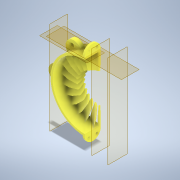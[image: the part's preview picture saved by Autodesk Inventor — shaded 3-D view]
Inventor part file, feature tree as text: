
AUTODESK INVENTOR PART (.ipt)
format: ipt  version: 2021.2 (Build 252289000, 289)  size: 1,402,368 bytes
history: native  units: in
note: dims shown in document units (in); Inventor stores cm internally (conversion verified against a paired STEP export)
features: sketch x11, extrude x10, plane x5, pattern_circular x3, fillet x2, loft x1, other x1
ambient origin geometry x8: Origin, YZ Plane, XZ Plane, XY Plane, X Axis, Y Axis, Z Axis, Center Point
bodies: Solid1 (feature_tree)
feature tree (33):
  extrude  "Extrusion1"  Depth=4.25in
  plane  "Work Plane2"
  extrude  "Extrusion3"  Depth=2.125in
  fillet  "Fillet1"  Radius=0.25in
  extrude  "Extrusion4"  Depth=0.5in TaperAngle=0.0deg
  pattern_circular  "Circular Pattern2"  Count=2 Angle=360.0deg
  plane  "Work Plane3"
  extrude  "Extrusion5"  Depth=1.0in
  extrude  "Extrusion6"  Depth=0.5in
  fillet  "Fillet2"  [1 undecoded]
  extrude  "Extrusion7"  Depth=0.5in TaperAngle=0.0deg
  pattern_circular  "Circular Pattern3"  [2 undecoded]
  plane  "Work Plane4"
  plane  "Work Plane6"
  sketch  "Sketch13"  dims[d18=0.5in d19=0.0in d20=0.7874in d21=360.0deg]
  extrude  "Extrusion15"  Depth=1.0in
  loft  "Loft5"
  pattern_circular  "Circular Pattern9"  Count=6 Angle=360.0deg
  extrude  "Extrusion16"  Depth=1.0in
  extrude  "Extrusion17"  Depth=0.125in
  plane  "Work Plane7"
  extrude  "Extrusion18"  Depth=1.0in
  sketch  "Sketch1"  dims[d0=4.0in d1=4.25in]
  sketch  "Sketch3"  dims[d2=1.0in d3=0.0in d10=2.125in d11=0.25in]
  sketch  "Sketch4"  dims[d12=0.0in d13=0.5in d14=0.0in]
  sketch  "Sketch5"  dims[d15=0.5in]
  sketch  "Sketch6"  dims[d16=0.125in]
  sketch  "Sketch7"  dims[d17=0.2in]
  sketch  "Sketch16"  dims[d23=-2.125in d24=1.0in]
  other  "Edges5"
  sketch  "Sketch18"  dims[d25=0.25in d26=0.5in d27=0.0in]
  sketch  "Sketch19"  dims[d28=0.1in d29=0.0in d30=0.5in d31=0.0in]
  sketch  "Sketch20"  dims[d32=0.5in d33=0.25in d34=0.2in d35=0.5in d36=0.0in d37=2.3622in d38=360.0deg d40=0.25in d41=0.125in d42=0.25in d43=0.2in d49=0.5in d75=1.5in d111=0.5in d112=0.0312in d113=0.5in d114=0.0in d115=0.0in d116=90.0deg d117=0.0in d118=90.0deg d119=9.4488in d120=360.0deg d122=1.8625in d123=0.0in d124=0.0777in d125=0.0in d126=0.0in d127=1.95in d128=1.0in d129=0.0in d79=0.5in d80=0.0344in d81=0.5in d82=0.0344in]
note: 3 required parameter values undecoded (feature->parameter linkage not recoverable at this tier; creation-order binding heuristic only, values carry confidence <= 0.55)
